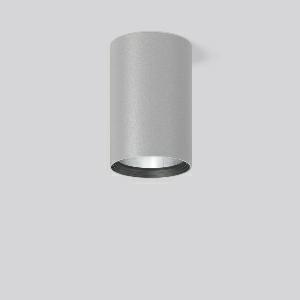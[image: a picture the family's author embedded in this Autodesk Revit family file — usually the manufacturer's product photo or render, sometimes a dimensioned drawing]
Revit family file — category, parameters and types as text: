
# Revit family: heledon_maxi_a_931224_004_3_76_59bf
name_source: partatom
category: Lighting Fixtures
units: mm (PartAtom-declared; Revit-internal decimal feet)

## family parameters
Cut with Voids When Loaded = No
Host = Face
Light Source = No
Part Type = Normal
Room Calculation Point = No
Round Connector Dimension = Use Diameter
Shared = No

## types (1)
- HELEDON maxi A (1 x LED Modul 935, 4350 lm, 3500)
    Apparent Load = 35 VA
    Approval mark = CE
    CIE Flux Codes = 100 100 100 100 100
    Color Rendering = 92
    Color Temperature = 3500
    Default Elevation = 1800 mm
    Description = Series: HELEDON maxi
Cylindrical surface-mounted downlight. Housing: die-cast aluminium, powder-coated. Internal ceiling frame polycarbonate with bayonet mounting. Black plastic ring and recessed LED to prevent glare from the side. Optical assembly with reflector made of MIRO-Silver with 98% total light reflection for outstanding efficiency - can be changed without tools. Best colour rendering index Ra>90. Suitable for Ceiling mounting. Easy installation with a separate ceiling frame with bayonet mounting and plug connection. Driver integrated. Connected via plug-in connector. High quality converter without flickering and stroboscopic effect. The following accessories can be mounted without use of tools: interchangeable lenses, decorative glasses, honeycomb louvre, clear and frosted diffusers, white interchangeable plastic ring. 
Colour: silver
Diameter: 123 mm
Height: 183 mm
Lamp: LED
Socket: without socket
Colour temperature: 3500K
Colour rendering index (CRI): 92
System power: 35 W
Rated luminous flux: 4350 lm
Luminous efficiency: 124 lm/W
Control gear: Converter, dimmable, DALI
Protection class: I
Type of protection: IP 20
    Height = 183 mm
    Lamp = 1 x LED Modul 935
    Lamp Light Flux = 4350 lm
    Lamp count = 1
    Length = 123 mm
    Lifetime = 50000 h
    Luminous efficacy = 124 lm/W
    Manufacturer = RZB
    ModVariant = No
    Model = 931224.004.3.76
    Mounting Place = Ceiling
    Mounting Type = Surface mounted
    Number of Poles = 1
    OnlyDefault = Yes
    Power Factor = 1
    Product Name = HELEDON maxi A
    Product group = Surface mounted downlights
    ProductGroupID = 302
    Protection Class = Protection class I
    Protection Degree = IP 20
    RLX_Detail_Level = 1
    RLX_Emergency_Light_Flux = 0 lm
    RLX_Emergency_Type = 0
    RLX_Emergency_Type_DB = No
    RlxData = <blob elided: 98013 chars, md5=6fa0de5c>
    Socket = socket
    Standby Power = 0 W
    System Light Flux = 4350 lm
    System Power = 35 W
    Type Comments = Product without accessories
    Type Image = 931192.004.jpg
    URL = http://relux.com
    VarID = ---
    Voltage = 230 V
    Voltage Range = 220-240 V
    Weight = 0.00 kg
    Width = 0 mm  [stored 0 ft]

note: [stored X ft] marks values corroborated as IEEE doubles in the binary element streams (Revit-internal decimal feet)

## geometry (parser evidence)
native form markers: Blend x4, Sweep x12
no freeform markers — native parametric forms only
